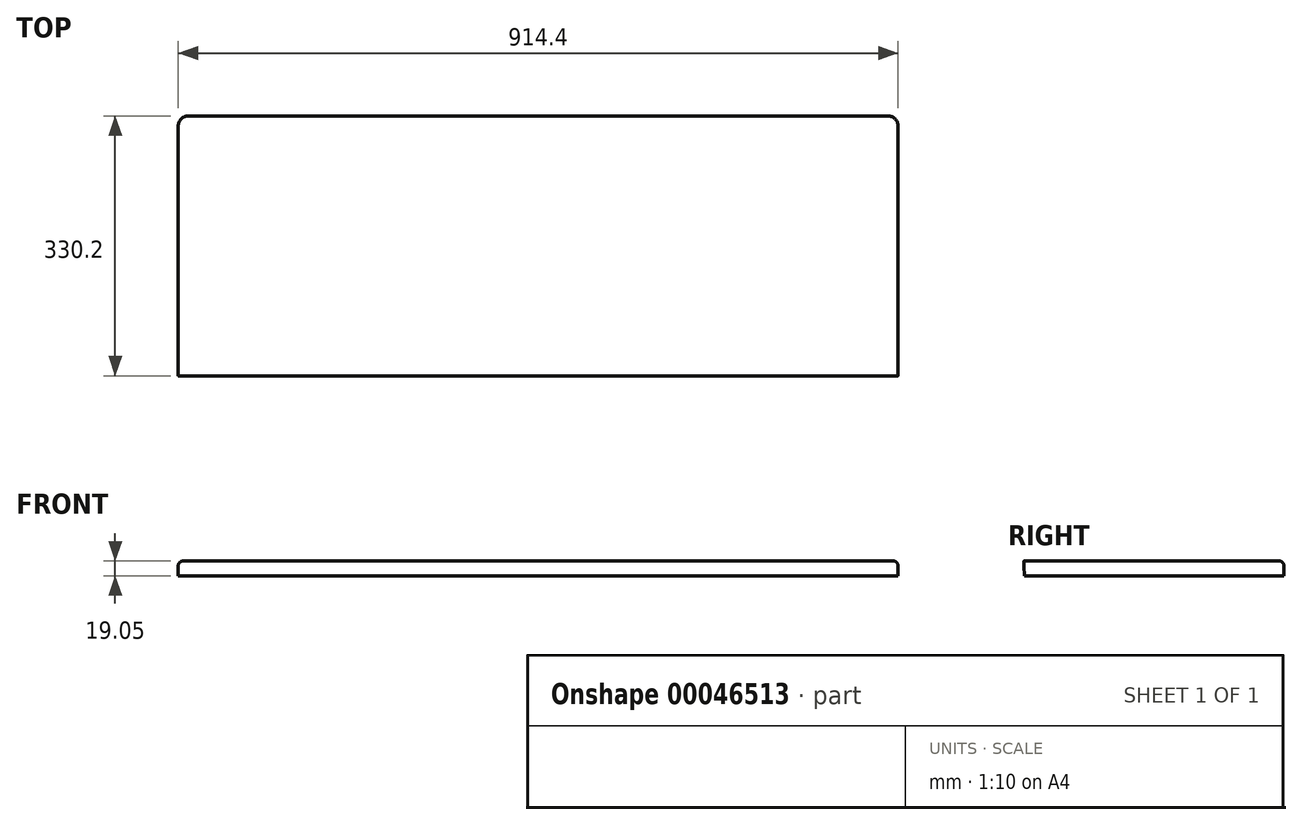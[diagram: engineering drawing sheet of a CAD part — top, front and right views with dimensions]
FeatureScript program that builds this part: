
annotation { "Feature Type Name" : "Feature", "Feature Type Description" : "" }
export const myFeature = defineFeature(function(context is Context, id is Id, definition is map)
    precondition{}
    {
        {
            var Q0;
            Q0=qCreatedBy(makeId("Right.planeOp"),FACE);
            var sketch = newSketch(context, id + "F0", { "sketchPlane" : qUnion([Q0])});
            skLineSegment(sketch, "E0.bottom", {"start": v(-146.77, -26.1) * mm, "end": v(183.43, -26.1) * mm});
            skLineSegment(sketch, "E0.top", {"start": v(-146.25, -45.15) * mm, "end": v(183.43, -45.15) * mm});
            skLineSegment(sketch, "E0.left", {"start": v(-146.77, -26.1) * mm, "end": v(-146.25, -45.15) * mm});
            skLineSegment(sketch, "E0.right", {"start": v(183.43, -26.1) * mm, "end": v(183.43, -45.15) * mm});
            skSolve(sketch);
        }
        {
            var Q0;
            Q0=makeQuery(id+"F0.imprint","IMPRINT",FACE,{"disambiguationData":[TD([[makeQuery(id+"F0.imprint","IMPRINT",EDGE,{"derivedFrom":sQuery(id+"F0.wireOp",EDGE,"E0.bottom")}),-1.0]])]});
            extrude(context, id + "F1", {"entities" : qUnion([Q0]), "depth" : 914.4 * mm});
        }
        {
            var Q0;
            Q0=makeQuery(id+"F1.opExtrude","CAP_EDGE",EDGE,{"disambiguationData":[OSD([sQuery(id+"F0.wireOp",EDGE,"E0.bottom")])],"isStart":true});
            var Q1;
            Q1=makeQuery(id+"F1.opExtrude","SWEPT_EDGE",EDGE,{"disambiguationData":[OSD([sQuery(id+"F0.wireOp",EDGE,"E0.bottom"),sQuery(id+"F0.wireOp",EDGE,"E0.right")])]});
            var Q2;
            Q2=makeQuery(id+"F1.opExtrude","CAP_EDGE",EDGE,{"disambiguationData":[OSD([sQuery(id+"F0.wireOp",EDGE,"E0.bottom")])],"isStart":false});
            fillet(context, id + "F2", {"entities" : qUnion([Q0, Q1, Q2]), "radius" : 6.35 * mm, "tangentPropagation" : true, "allowEdgeOverflow" : false});
        }
        {
            var Q0;
            Q0=makeQuery(id+"F1.opExtrude","CAP_EDGE",EDGE,{"disambiguationData":[OSD([sQuery(id+"F0.wireOp",EDGE,"E0.right")])],"isStart":false});
            var Q1;
            Q1=makeQuery(id+"F1.opExtrude","CAP_EDGE",EDGE,{"disambiguationData":[OSD([sQuery(id+"F0.wireOp",EDGE,"E0.right")])],"isStart":true});
            fillet(context, id + "F3", {"entities" : qUnion([Q0, Q1]), "radius" : 12.7 * mm, "tangentPropagation" : true, "allowEdgeOverflow" : false});
        }
    });
